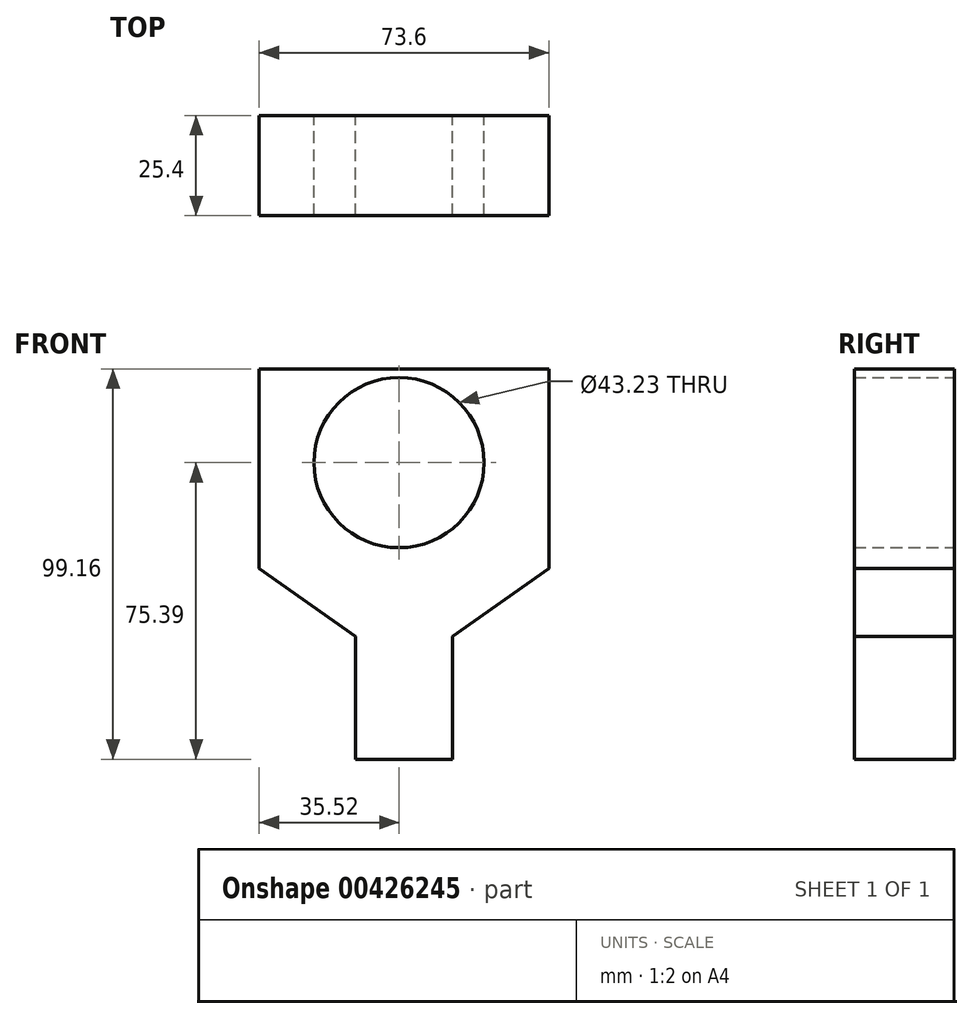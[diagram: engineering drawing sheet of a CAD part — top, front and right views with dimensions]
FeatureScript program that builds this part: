
annotation { "Feature Type Name" : "Feature", "Feature Type Description" : "" }
export const myFeature = defineFeature(function(context is Context, id is Id, definition is map)
    precondition{}
    {
        {
            var Q0;
            Q0=qCreatedBy(makeId("Front.planeOp"),FACE);
            var sketch = newSketch(context, id + "F0", { "sketchPlane" : qUnion([Q0])});
            skCircle(sketch, "E0", {"center": v(0, 0) * mm, "radius": 21.61 * mm});
            skLineSegment(sketch, "E1", {"start": v(-35.52, 0) * mm, "end": v(-35.52, -26.83) * mm});
            skLineSegment(sketch, "E2", {"start": v(-35.52, -26.83) * mm, "end": v(-10.99, -44.2) * mm});
            skLineSegment(sketch, "E3", {"start": v(-10.99, -44.2) * mm, "end": v(-10.99, -75.39) * mm});
            skLineSegment(sketch, "E4", {"start": v(-10.99, -75.39) * mm, "end": v(13.54, -75.39) * mm});
            skLineSegment(sketch, "E5", {"start": v(13.54, -75.39) * mm, "end": v(13.54, -44.2) * mm});
            skLineSegment(sketch, "E6", {"start": v(13.54, -44.2) * mm, "end": v(38.08, -26.83) * mm});
            skLineSegment(sketch, "E7", {"start": v(38.08, -26.83) * mm, "end": v(38.08, 0) * mm});
            skLineSegment(sketch, "E8", {"start": v(38.08, 0) * mm, "end": v(38.08, 23.77) * mm});
            skLineSegment(sketch, "E9", {"start": v(38.08, 23.77) * mm, "end": v(-35.52, 23.77) * mm});
            skLineSegment(sketch, "E10", {"start": v(-35.52, 23.77) * mm, "end": v(-35.52, 0) * mm});
            skSolve(sketch);
        }
        {
            var Q0;
            Q0=makeQuery(id+"F0.imprint","IMPRINT",FACE,{"disambiguationData":[TD([[makeQuery(id+"F0.imprint","IMPRINT",EDGE,{"derivedFrom":sQuery(id+"F0.wireOp",EDGE,"E0")}),-1.0]])]});
            extrude(context, id + "F1", {"entities" : qUnion([Q0]), "depth" : 25.4 * mm, "offsetDistance" : 25.4 * mm});
        }
    });
